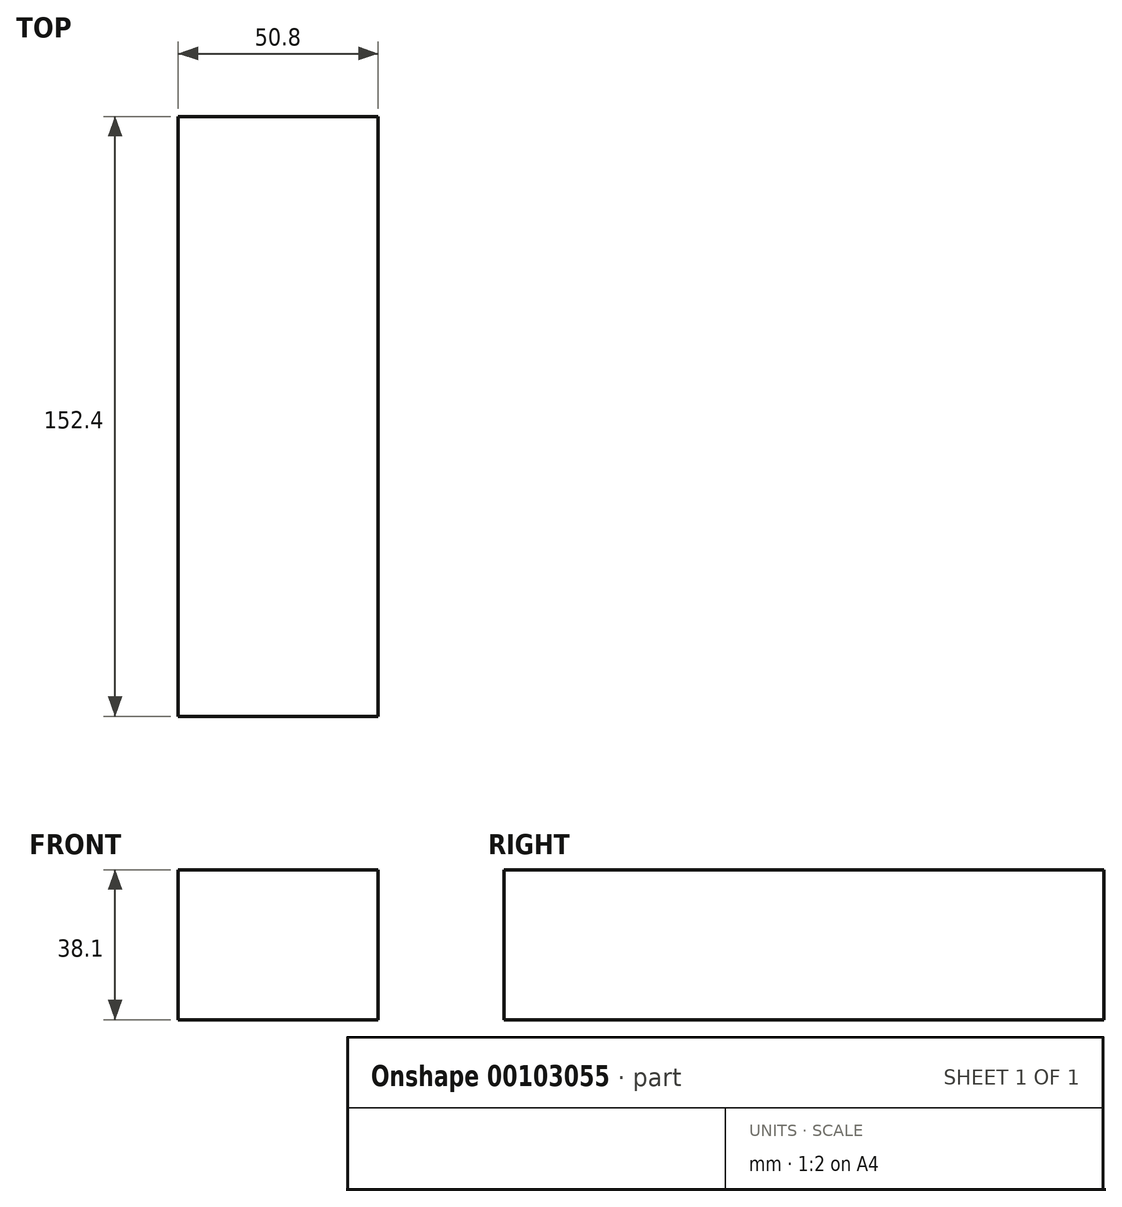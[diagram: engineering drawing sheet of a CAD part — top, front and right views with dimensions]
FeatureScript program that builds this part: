
annotation { "Feature Type Name" : "Feature", "Feature Type Description" : "" }
export const myFeature = defineFeature(function(context is Context, id is Id, definition is map)
    precondition{}
    {
        {
            var Q0;
            Q0=qCreatedBy(makeId("Top.planeOp"),FACE);
            var sketch = newSketch(context, id + "F0", { "sketchPlane" : qUnion([Q0])});
            skLineSegment(sketch, "E0.top", {"start": v(-35.16, -37.95) * mm, "end": v(15.64, -37.95) * mm});
            skLineSegment(sketch, "E1", {"start": v(-35.16, 114.45) * mm, "end": v(-35.16, 29.78) * mm});
            skLineSegment(sketch, "E2", {"start": v(-35.16, -4.09) * mm, "end": v(-35.16, 29.78) * mm});
            skLineSegment(sketch, "E3", {"start": v(-35.16, -37.95) * mm, "end": v(-35.16, -4.09) * mm});
            skLineSegment(sketch, "E4", {"start": v(15.64, 114.45) * mm, "end": v(15.64, -37.95) * mm});
            skLineSegment(sketch, "E5", {"start": v(-35.16, 114.45) * mm, "end": v(15.64, 114.45) * mm});
            skPoint(sketch, "E0.right.start.orphan", {"position": v(66.44, 114.45) * mm});
            skPoint(sketch, "E6.orphan", {"position": v(66.44, -37.95) * mm});
            skSolve(sketch);
        }
        {
            var Q0;
            Q0=makeQuery(id+"F0.imprint","IMPRINT",FACE,{"disambiguationData":[TD([[makeQuery(id+"F0.imprint","IMPRINT",EDGE,{"derivedFrom":sQuery(id+"F0.wireOp",EDGE,"E0.top")}),1.0]])]});
            extrude(context, id + "F1", {"entities" : qUnion([Q0]), "endBound" : BoundingType.SYMMETRIC, "depth" : 38.1 * mm});
        }
    });
